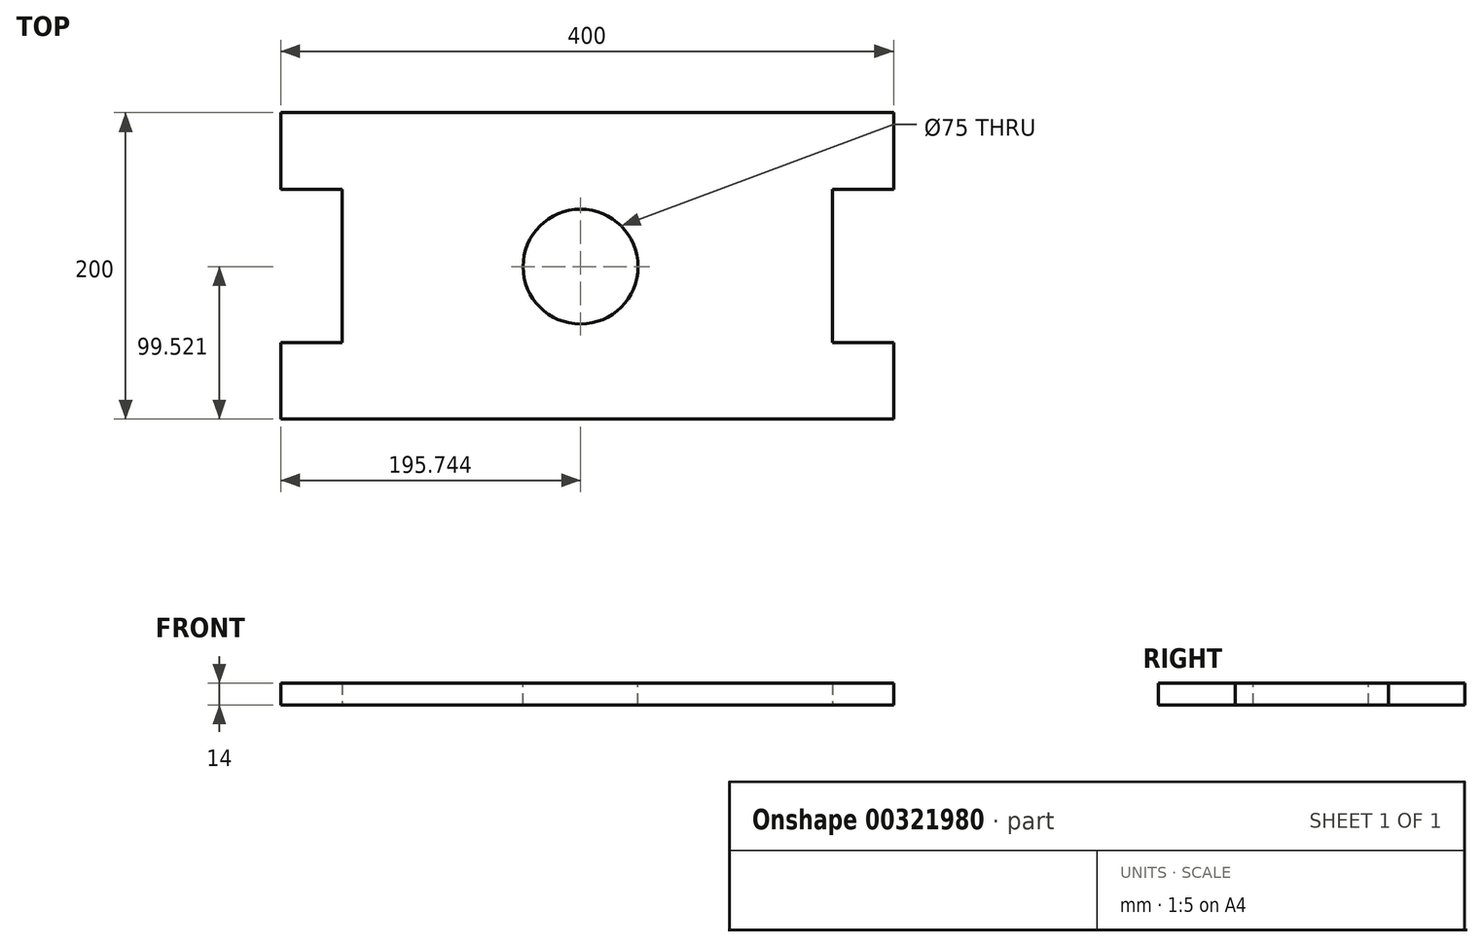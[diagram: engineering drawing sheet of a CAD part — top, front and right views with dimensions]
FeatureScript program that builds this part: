
annotation { "Feature Type Name" : "Feature", "Feature Type Description" : "" }
export const myFeature = defineFeature(function(context is Context, id is Id, definition is map)
    precondition{}
    {
        {
            var Q0;
            Q0=qCreatedBy(makeId("Top.planeOp"),FACE);
            var sketch = newSketch(context, id + "F0", { "sketchPlane" : qUnion([Q0])});
            skLineSegment(sketch, "E0.bottom", {"start": v(0, 0) * mm, "end": v(400, 0) * mm});
            skLineSegment(sketch, "E0.top", {"start": v(0, -200) * mm, "end": v(400, -200) * mm});
            skLineSegment(sketch, "E0.left", {"start": v(0, 0) * mm, "end": v(0, -200) * mm});
            skLineSegment(sketch, "E0.right", {"start": v(400, 0) * mm, "end": v(400, -200) * mm});
            skLineSegment(sketch, "E1.bottom", {"start": v(0, -50) * mm, "end": v(40, -50) * mm});
            skLineSegment(sketch, "E1.top", {"start": v(0, -150) * mm, "end": v(40, -150) * mm});
            skLineSegment(sketch, "E1.left", {"start": v(0, -50) * mm, "end": v(0, -150) * mm});
            skLineSegment(sketch, "E1.right", {"start": v(40, -50) * mm, "end": v(40, -150) * mm});
            skLineSegment(sketch, "E2", {"start": v(200, 0) * mm, "end": v(200, -200) * mm, "construction": true});
            skLineSegment(sketch, "E3", {"start": v(400, -100) * mm, "end": v(0, -100) * mm, "construction": true});
            skLineSegment(sketch, "E4.left", {"start": v(400, -50) * mm, "end": v(400, -150) * mm});
            skLineSegment(sketch, "E5.MirrorCS", {"start": v(360, -50) * mm, "end": v(360, -150) * mm});
            skLineSegment(sketch, "E6.MirrorCS", {"start": v(400, -150) * mm, "end": v(360, -150) * mm});
            skLineSegment(sketch, "E7.MirrorCS", {"start": v(400, -50) * mm, "end": v(360, -50) * mm});
            skSolve(sketch);
        }
        {
            var Q0;
            {var subQ6=sQuery(id+"F0.wireOp",EDGE,"E0.bottom");Q0=makeQuery(id+"F0.imprint","IMPRINT",FACE,{"disambiguationData":[TD([[makeQuery(id+"F0.imprint","IMPRINT",EDGE,{"derivedFrom":subQ6}),-1.0]])]});}
            extrude(context, id + "F1", {"entities" : qUnion([Q0]), "depth" : 14 * mm});
        }
        {
            var Q0;
            Q0=makeQuery(id+"F1.opExtrude","CAP_FACE",FACE,{"disambiguationData":[OSD([sQuery(id+"F0.wireOp",EDGE,"E0.bottom"),sQuery(id+"F0.wireOp",EDGE,"E0.top"),sQuery(id+"F0.wireOp",EDGE,"E0.left"),sQuery(id+"F0.wireOp",EDGE,"E0.right"),sQuery(id+"F0.wireOp",EDGE,"E1.bottom"),sQuery(id+"F0.wireOp",EDGE,"E1.top"),sQuery(id+"F0.wireOp",EDGE,"E1.right"),sQuery(id+"F0.wireOp",EDGE,"E5.MirrorCS"),sQuery(id+"F0.wireOp",EDGE,"E6.MirrorCS"),sQuery(id+"F0.wireOp",EDGE,"E7.MirrorCS")])],"isStart":false});
            var sketch = newSketch(context, id + "F2", { "sketchPlane" : qUnion([Q0])});
            skCircle(sketch, "E8", {"center": v(195.74, -100.48) * mm, "radius": 37.5 * mm});
            skSolve(sketch);
        }
        {
            var Q0;
            Q0 = qSketchRegion(id + "F2", true);
            extrude(context, id + "F3", {"entities" : qUnion([Q0]), "operationType" : NewBodyOperationType.REMOVE, "oppositeDirection" : true, "depth" : 14 * mm});
        }
    });
